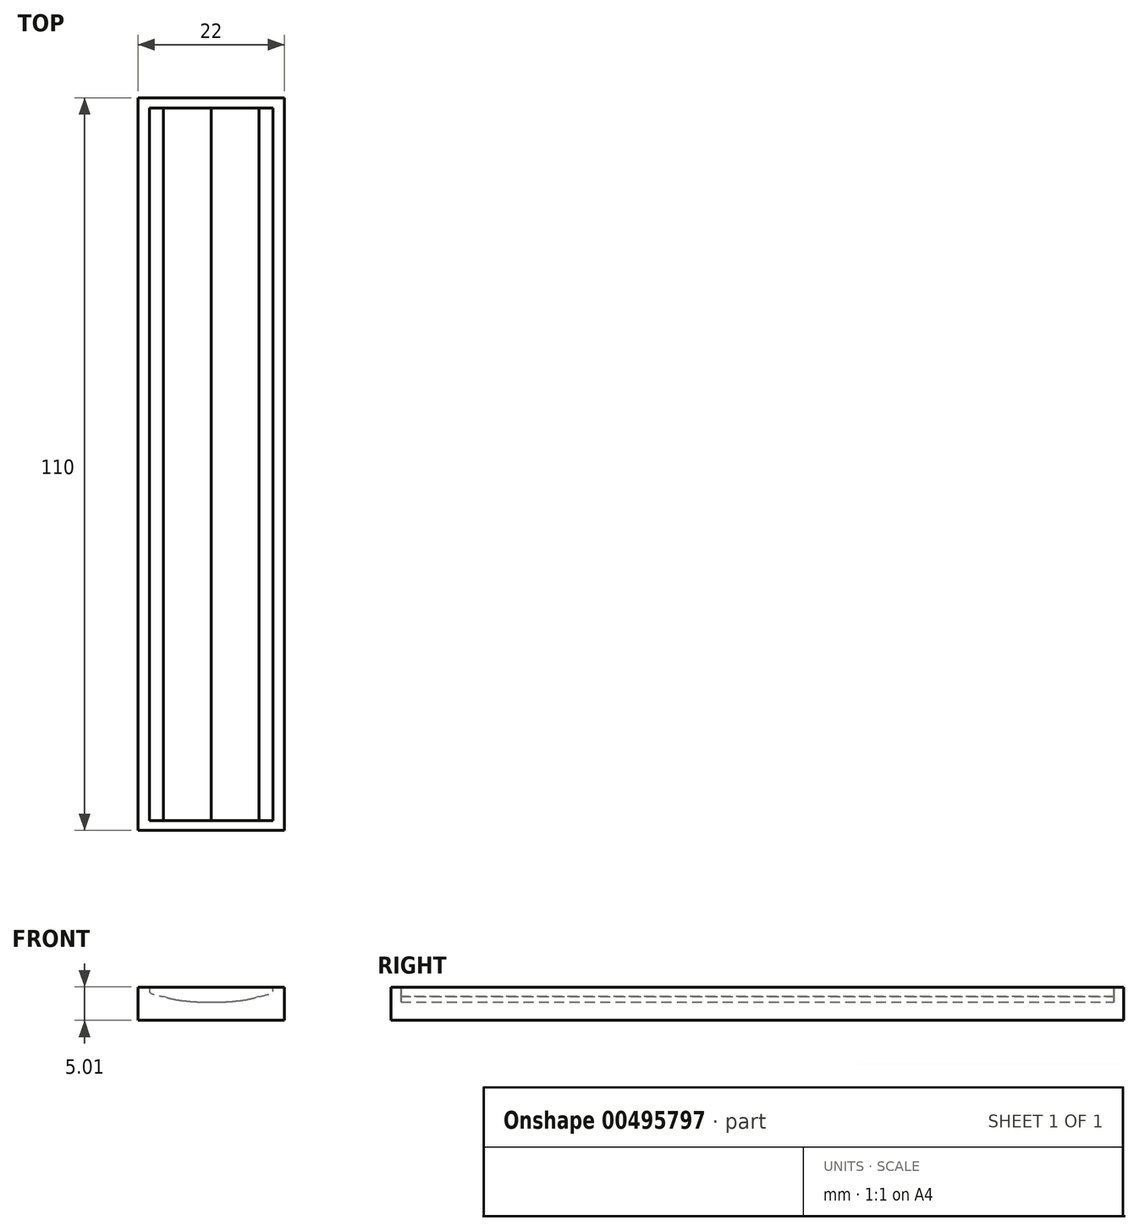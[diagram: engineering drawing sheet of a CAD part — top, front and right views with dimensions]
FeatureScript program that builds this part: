
annotation { "Feature Type Name" : "Feature", "Feature Type Description" : "" }
export const myFeature = defineFeature(function(context is Context, id is Id, definition is map)
    precondition{}
    {
        {
            var Q0;
            Q0=qCreatedBy(makeId("Front.planeOp"),FACE);
            var sketch = newSketch(context, id + "F0", { "sketchPlane" : qUnion([Q0])});
            skFitSpline(sketch, "E0", {"points": [v(0, 1.12) * mm, v(-1.8, 1.13) * mm, v(-5.1, 0.8) * mm, v(-7.18, 0.31) * mm]});
            skFitSpline(sketch, "E1", {"points": [v(-7.18, 0.31) * mm, v(-8.5, 0) * mm, v(-9.17, -0.33) * mm, v(-9.26, -1.12) * mm]});
            skLineSegment(sketch, "E2", {"start": v(-9.26, -1.12) * mm, "end": v(9.3, -1.12) * mm});
            skFitSpline(sketch, "E3", {"points": [v(9.27, -1.12) * mm, v(9.2, -0.33) * mm, v(8.5, 0) * mm, v(7.2, 0.3) * mm]});
            skFitSpline(sketch, "E4", {"points": [v(7.2, 0.3) * mm, v(5.11, 0.8) * mm, v(1.83, 1.12) * mm, v(0, 1.12) * mm]});
            skLineSegment(sketch, "E5", {"start": v(0.03, 1.12) * mm, "end": v(0, 1.12) * mm});
            skArc(sketch, "E6", {"start": v(-6.9, 0.38) * mm, "mid": v(-6.79, 0.56) * mm, "end": v(-6.6, 0.44) * mm});
            skArc(sketch, "E7", {"start": v(-5.4, 0.65) * mm, "mid": v(-5.28, 0.82) * mm, "end": v(-5.1, 0.7) * mm});
            skArc(sketch, "E8", {"start": v(-3.9, 0.86) * mm, "mid": v(-3.77, 1.02) * mm, "end": v(-3.6, 0.9) * mm});
            skArc(sketch, "E9", {"start": v(-2.4, 1) * mm, "mid": v(-2.27, 1.17) * mm, "end": v(-2.1, 1.03) * mm});
            skArc(sketch, "E10", {"start": v(0.6, 1.11) * mm, "mid": v(0.75, 1.26) * mm, "end": v(0.9, 1.1) * mm});
            skArc(sketch, "E11", {"start": v(2.1, 1.03) * mm, "mid": v(2.26, 1.17) * mm, "end": v(2.4, 1) * mm});
            skArc(sketch, "E12", {"start": v(3.6, 0.9) * mm, "mid": v(3.76, 1.02) * mm, "end": v(3.9, 0.86) * mm});
            skArc(sketch, "E13", {"start": v(-0.9, 1.1) * mm, "mid": v(-0.76, 1.26) * mm, "end": v(-0.6, 1.11) * mm});
            skArc(sketch, "E14", {"start": v(5.1, 0.7) * mm, "mid": v(5.27, 0.82) * mm, "end": v(5.4, 0.65) * mm});
            skPoint(sketch, "E15", {"position": v(6.74, 0.41) * mm});
            skArc(sketch, "E16", {"start": v(6.6, 0.44) * mm, "mid": v(6.78, 0.56) * mm, "end": v(6.9, 0.38) * mm});
            skSolve(sketch);
        }
        {
            var Q0;
            {var subQ15=sQuery(id+"F0.wireOp",EDGE,"E1");Q0=makeQuery(id+"F0.imprint","IMPRINT",FACE,{"disambiguationData":[TD([[makeQuery(id+"F0.imprint","IMPRINT",EDGE,{"derivedFrom":subQ15}),1.0]])]});}
            var Q1;
            {var subQ0=sQuery(id+"F0.wireOp",EDGE,"E6");Q1=makeQuery(id+"F0.imprint","IMPRINT",FACE,{"disambiguationData":[TD([[makeQuery(id+"F0.imprint","IMPRINT",EDGE,{"derivedFrom":subQ0}),-1.0]])]});}
            var Q2;
            {var subQ0=sQuery(id+"F0.wireOp",EDGE,"E7");Q2=makeQuery(id+"F0.imprint","IMPRINT",FACE,{"disambiguationData":[TD([[makeQuery(id+"F0.imprint","IMPRINT",EDGE,{"derivedFrom":subQ0}),-1.0]])]});}
            var Q3;
            {var subQ0=sQuery(id+"F0.wireOp",EDGE,"E8");Q3=makeQuery(id+"F0.imprint","IMPRINT",FACE,{"disambiguationData":[TD([[makeQuery(id+"F0.imprint","IMPRINT",EDGE,{"derivedFrom":subQ0}),-1.0]])]});}
            var Q4;
            {var subQ0=sQuery(id+"F0.wireOp",EDGE,"E9");Q4=makeQuery(id+"F0.imprint","IMPRINT",FACE,{"disambiguationData":[TD([[makeQuery(id+"F0.imprint","IMPRINT",EDGE,{"derivedFrom":subQ0}),-1.0]])]});}
            var Q5;
            {var subQ0=sQuery(id+"F0.wireOp",EDGE,"E13");Q5=makeQuery(id+"F0.imprint","IMPRINT",FACE,{"disambiguationData":[TD([[makeQuery(id+"F0.imprint","IMPRINT",EDGE,{"derivedFrom":subQ0}),-1.0]])]});}
            var Q6;
            {var subQ0=sQuery(id+"F0.wireOp",EDGE,"E10");Q6=makeQuery(id+"F0.imprint","IMPRINT",FACE,{"disambiguationData":[TD([[makeQuery(id+"F0.imprint","IMPRINT",EDGE,{"derivedFrom":subQ0}),-1.0]])]});}
            var Q7;
            {var subQ0=sQuery(id+"F0.wireOp",EDGE,"E11");Q7=makeQuery(id+"F0.imprint","IMPRINT",FACE,{"disambiguationData":[TD([[makeQuery(id+"F0.imprint","IMPRINT",EDGE,{"derivedFrom":subQ0}),-1.0]])]});}
            var Q8;
            {var subQ0=sQuery(id+"F0.wireOp",EDGE,"E12");Q8=makeQuery(id+"F0.imprint","IMPRINT",FACE,{"disambiguationData":[TD([[makeQuery(id+"F0.imprint","IMPRINT",EDGE,{"derivedFrom":subQ0}),-1.0]])]});}
            var Q9;
            {var subQ0=sQuery(id+"F0.wireOp",EDGE,"E14");Q9=makeQuery(id+"F0.imprint","IMPRINT",FACE,{"disambiguationData":[TD([[makeQuery(id+"F0.imprint","IMPRINT",EDGE,{"derivedFrom":subQ0}),-1.0]])]});}
            var Q10;
            {var subQ0=sQuery(id+"F0.wireOp",EDGE,"E16");Q10=makeQuery(id+"F0.imprint","IMPRINT",FACE,{"disambiguationData":[TD([[makeQuery(id+"F0.imprint","IMPRINT",EDGE,{"derivedFrom":subQ0}),-1.0]])]});}
            extrude(context, id + "F1", {"entities" : qUnion([Q0, Q1, Q2, Q3, Q4, Q5, Q6, Q7, Q8, Q9, Q10]), "endBound" : BoundingType.SYMMETRIC, "depth" : 101 * mm});
        }
        {
            var Q0;
            {var subQ15=sQuery(id+"F0.wireOp",EDGE,"E1");Q0=makeQuery(id+"F0.imprint","IMPRINT",FACE,{"disambiguationData":[TD([[makeQuery(id+"F0.imprint","IMPRINT",EDGE,{"derivedFrom":subQ15}),1.0]])]});}
            extrude(context, id + "F2", {"entities" : qUnion([Q0]), "operationType" : NewBodyOperationType.ADD, "endBound" : BoundingType.SYMMETRIC, "depth" : 107 * mm});
        }
        {
            var Q0;
            {var subQ0=sQuery(id+"F0.wireOp",EDGE,"E2");Q0=makeQuery(id+"F2.boolean.opBoolean","MERGE",FACE,{"derivedFrom":[makeQuery(id+"F1.opExtrude","SWEPT_FACE",FACE,{"disambiguationData":[OSD([subQ0])]}),makeQuery(id+"F2.opExtrude","SWEPT_FACE",FACE,{"disambiguationData":[OSD([subQ0])]})]});}
            var sketch = newSketch(context, id + "F3", { "sketchPlane" : qUnion([Q0])});
            skLineSegment(sketch, "E17.bottom", {"start": v(-11, 55) * mm, "end": v(11, 55) * mm});
            skLineSegment(sketch, "E17.top", {"start": v(-11, -55) * mm, "end": v(11, -55) * mm});
            skLineSegment(sketch, "E17.left", {"start": v(-11, 55) * mm, "end": v(-11, -55) * mm});
            skLineSegment(sketch, "E17.right", {"start": v(11, 55) * mm, "end": v(11, -55) * mm});
            skLineSegment(sketch, "E18.0.0", {"start": v(-9.26, 53.5) * mm, "end": v(-9.26, -53.5) * mm});
            skLineSegment(sketch, "E18.0.1", {"start": v(-9.26, -53.5) * mm, "end": v(9.27, -53.5) * mm});
            skLineSegment(sketch, "E18.0.2", {"start": v(9.27, -53.5) * mm, "end": v(9.27, 53.5) * mm});
            skLineSegment(sketch, "E18.0.3", {"start": v(9.27, 53.5) * mm, "end": v(-9.26, 53.5) * mm});
            skPoint(sketch, "E19", {"position": v(-9.26, 0) * mm});
            skPoint(sketch, "E20", {"position": v(-11, 0) * mm});
            skPoint(sketch, "E21", {"position": v(0, 53.5) * mm});
            skPoint(sketch, "E22", {"position": v(0, 55) * mm});
            skSolve(sketch);
        }
        {
            var Q0;
            Q0=makeQuery(id+"F3.imprint","IMPRINT",FACE,{"disambiguationData":[TD([[makeQuery(id+"F3.imprint","IMPRINT",EDGE,{"derivedFrom":sQuery(id+"F3.wireOp",EDGE,"E17.bottom")}),-1.0]])]});
            var Q1;
            Q1=makeQuery(id+"F3.imprint","IMPRINT",FACE,{"disambiguationData":[TD([[makeQuery(id+"F3.imprint","IMPRINT",EDGE,{"derivedFrom":sQuery(id+"F3.wireOp",EDGE,"E18.0.0")}),1.0]])]});
            extrude(context, id + "F4", {"entities" : qUnion([Q0, Q1]), "oppositeDirection" : true, "depth" : 5 * mm});
        }
        {
            var Q0;
            Q0=makeQuery(id+"F1.opExtrude","SWEPT_BODY",BODY,{"disambiguationData":[OSD([sQuery(id+"F0.wireOp",EDGE,"E0"),sQuery(id+"F0.wireOp",EDGE,"E1"),sQuery(id+"F0.wireOp",EDGE,"E2"),sQuery(id+"F0.wireOp",EDGE,"E3"),sQuery(id+"F0.wireOp",EDGE,"E4"),sQuery(id+"F0.wireOp",EDGE,"E5"),sQuery(id+"F0.wireOp",EDGE,"E6"),sQuery(id+"F0.wireOp",EDGE,"E7"),sQuery(id+"F0.wireOp",EDGE,"E8"),sQuery(id+"F0.wireOp",EDGE,"E9"),sQuery(id+"F0.wireOp",EDGE,"E10"),sQuery(id+"F0.wireOp",EDGE,"E11"),sQuery(id+"F0.wireOp",EDGE,"E12"),sQuery(id+"F0.wireOp",EDGE,"E13"),sQuery(id+"F0.wireOp",EDGE,"E14"),sQuery(id+"F0.wireOp",EDGE,"E16")])]});
            var Q1;
            Q1=makeQuery(id+"F4.opExtrude","SWEPT_BODY",BODY,{"disambiguationData":[OSD([sQuery(id+"F3.wireOp",EDGE,"E17.bottom"),sQuery(id+"F3.wireOp",EDGE,"E17.top"),sQuery(id+"F3.wireOp",EDGE,"E17.left"),sQuery(id+"F3.wireOp",EDGE,"E17.right")])]});
            booleanBodies(context, id + "F5", {"operationType" : BooleanOperationType.SUBTRACTION, "tools" : qUnion([Q0]), "targets" : qUnion([Q1])});
        }
        {
            var Q0;
            Q0=makeQuery(id+"F4.opExtrude","SWEPT_BODY",BODY,{"disambiguationData":[OSD([sQuery(id+"F3.wireOp",EDGE,"E17.bottom"),sQuery(id+"F3.wireOp",EDGE,"E17.top"),sQuery(id+"F3.wireOp",EDGE,"E17.left"),sQuery(id+"F3.wireOp",EDGE,"E17.right")])]});
            var Q1;
            Q1=makeQuery(id+"F4.opExtrude","CAP_EDGE",EDGE,{"disambiguationData":[OSD([sQuery(id+"F3.wireOp",EDGE,"E17.right")])],"isStart":false});
            transform(context, id + "F6", {"entities" : qUnion([Q0]), "transformType" : TransformType.ROTATION, "transformAxis" : qUnion([Q1]), "angle" : 180 * degree, "makeCopy" : false});
        }
    });
